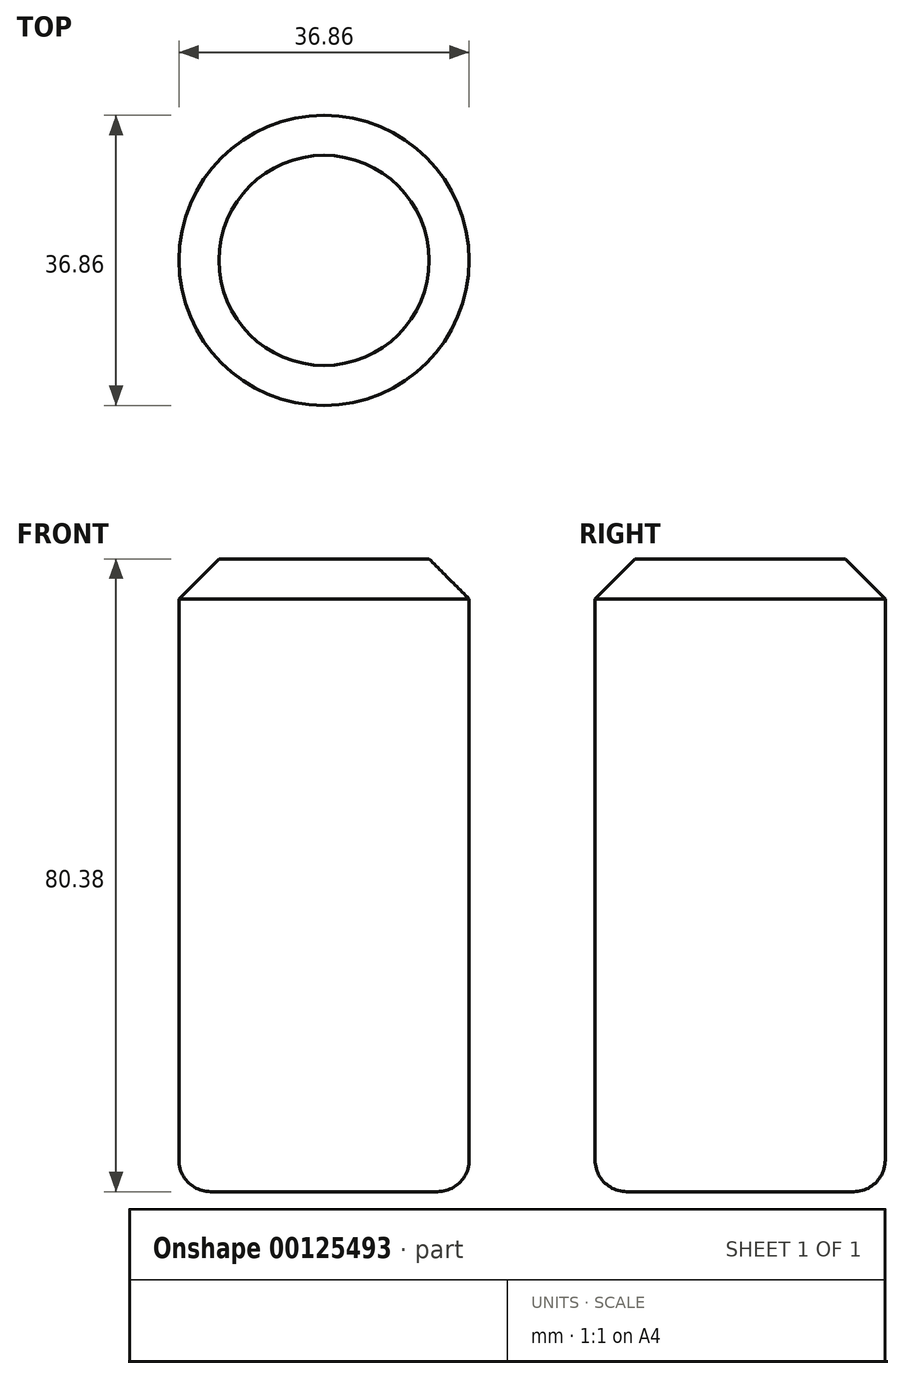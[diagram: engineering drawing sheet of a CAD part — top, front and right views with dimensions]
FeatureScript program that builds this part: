
annotation { "Feature Type Name" : "Feature", "Feature Type Description" : "" }
export const myFeature = defineFeature(function(context is Context, id is Id, definition is map)
    precondition{}
    {
        {
            var Q0;
            Q0=qCreatedBy(makeId("Top.planeOp"),FACE);
            var sketch = newSketch(context, id + "F0", { "sketchPlane" : qUnion([Q0])});
            skCircle(sketch, "E0", {"center": v(0, 0) * mm, "radius": 18.43 * mm});
            skSolve(sketch);
        }
        {
            var Q0;
            Q0=makeQuery(id+"F0.imprint","IMPRINT",FACE,{"disambiguationData":[TD([[makeQuery(id+"F0.imprint","IMPRINT",EDGE,{"derivedFrom":sQuery(id+"F0.wireOp",EDGE,"E0")}),1.0]])]});
            extrude(context, id + "F1", {"entities" : qUnion([Q0]), "depth" : 80.38 * mm});
        }
        {
            var Q0;
            Q0=makeQuery(id+"F1.opExtrude","CAP_EDGE",EDGE,{"disambiguationData":[OSD([sQuery(id+"F0.wireOp",EDGE,"E0")])],"isStart":false});
            chamfer(context, id + "F2", {"entities" : qUnion([Q0]), "width" : 5.08 * mm, "tangentPropagation" : true});
        }
        {
            var Q0;
            Q0=makeQuery(id+"F1.opExtrude","CAP_EDGE",EDGE,{"disambiguationData":[OSD([sQuery(id+"F0.wireOp",EDGE,"E0")])],"isStart":true});
            fillet(context, id + "F3", {"entities" : qUnion([Q0]), "radius" : 4 * mm, "tangentPropagation" : true, "allowEdgeOverflow" : false});
        }
    });
